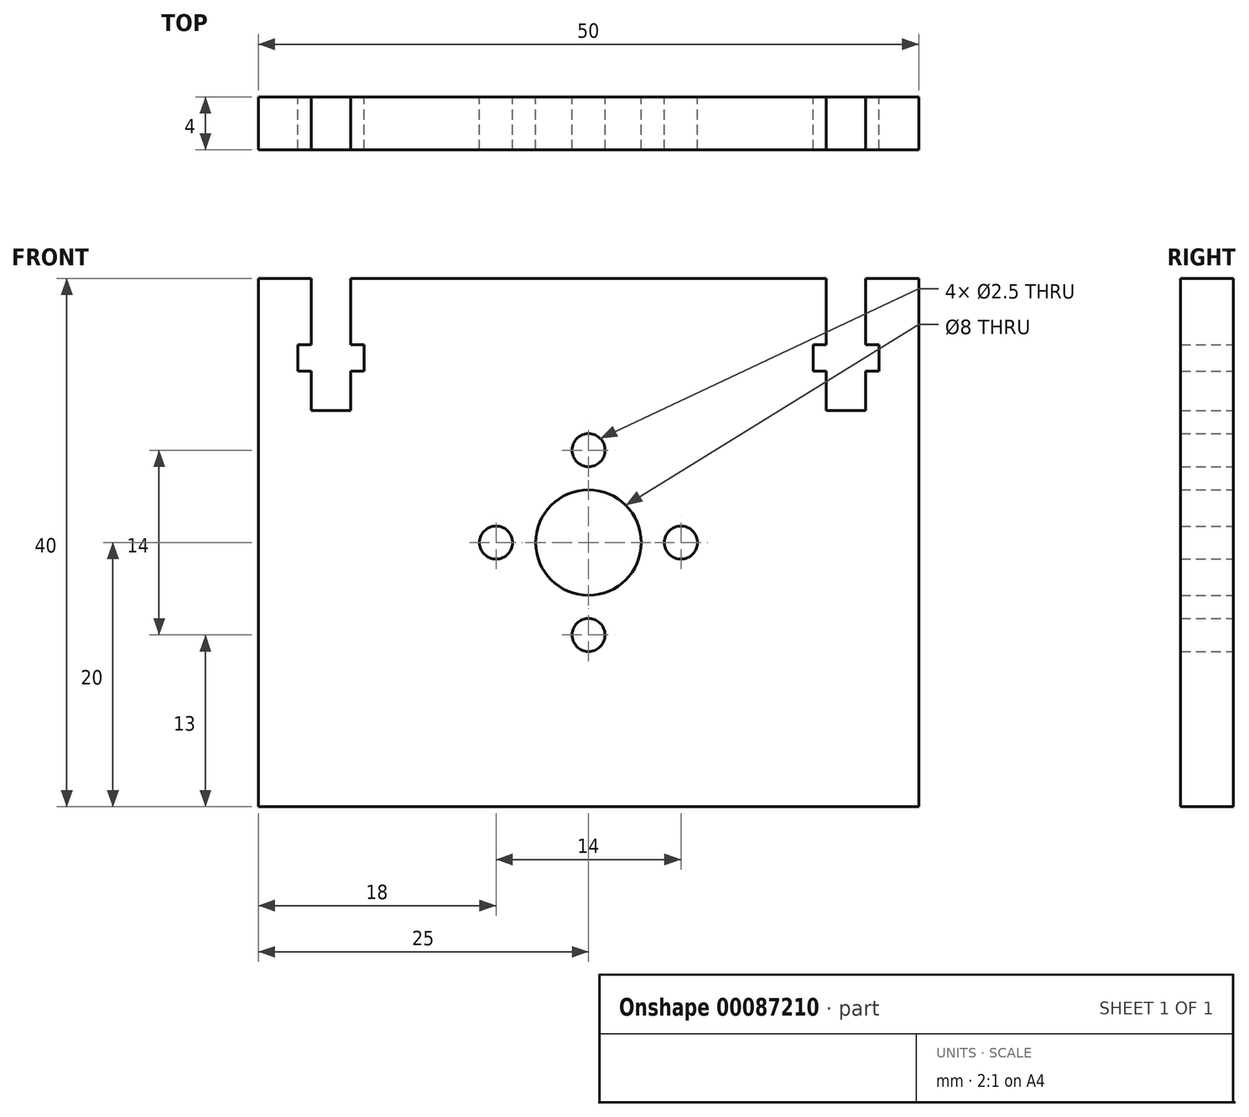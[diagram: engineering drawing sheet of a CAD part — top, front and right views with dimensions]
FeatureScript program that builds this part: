
annotation { "Feature Type Name" : "Feature", "Feature Type Description" : "" }
export const myFeature = defineFeature(function(context is Context, id is Id, definition is map)
    precondition{}
    {
        {
            var Q0;
            Q0=qCreatedBy(makeId("Front.planeOp"),FACE);
            var sketch = newSketch(context, id + "F0", { "sketchPlane" : qUnion([Q0])});
            skLineSegment(sketch, "E0.bottom", {"start": v(-46, 40) * mm, "end": v(-42, 40) * mm});
            skLineSegment(sketch, "E0.top", {"start": v(-46, 0) * mm, "end": v(4, 0) * mm});
            skLineSegment(sketch, "E0.left", {"start": v(-46, 40) * mm, "end": v(-46, 0) * mm});
            skLineSegment(sketch, "E0.right", {"start": v(4, 40) * mm, "end": v(4, 0) * mm});
            skLineSegment(sketch, "E1.left", {"start": v(4, 40) * mm, "end": v(4, 35) * mm});
            skLineSegment(sketch, "E1.right", {"start": v(0, 40) * mm, "end": v(0, 35) * mm});
            skLineSegment(sketch, "E2.top", {"start": v(1, 33) * mm, "end": v(0, 33) * mm});
            skLineSegment(sketch, "E2.right", {"start": v(-4, 35) * mm, "end": v(-4, 33) * mm});
            skLineSegment(sketch, "E3", {"start": v(-3, 40) * mm, "end": v(-3, 35) * mm});
            skLineSegment(sketch, "E4", {"start": v(-3, 33) * mm, "end": v(-3, 30) * mm});
            skLineSegment(sketch, "E5", {"start": v(0, 33) * mm, "end": v(0, 30) * mm});
            skLineSegment(sketch, "E6", {"start": v(0, 30) * mm, "end": v(-3, 30) * mm});
            skLineSegment(sketch, "E7.trimOffspring", {"start": v(-3, 35) * mm, "end": v(-4, 35) * mm});
            skLineSegment(sketch, "E8.trimOffspring", {"start": v(-3, 33) * mm, "end": v(-4, 33) * mm});
            skLineSegment(sketch, "E9.trimOffspring", {"start": v(0, 40) * mm, "end": v(4, 40) * mm});
            skLineSegment(sketch, "E10.top", {"start": v(-42, 30) * mm, "end": v(-39, 30) * mm});
            skLineSegment(sketch, "E10.left", {"start": v(-42, 40) * mm, "end": v(-42, 35) * mm});
            skLineSegment(sketch, "E10.right", {"start": v(-39, 40) * mm, "end": v(-39, 35) * mm});
            skPoint(sketch, "E11", {"position": v(-39, 35) * mm});
            skPoint(sketch, "E12", {"position": v(-39, 33) * mm});
            skLineSegment(sketch, "E13.bottom", {"start": v(-38, 35) * mm, "end": v(-39, 35) * mm});
            skLineSegment(sketch, "E13.top", {"start": v(-38, 33) * mm, "end": v(-39, 33) * mm});
            skLineSegment(sketch, "E13.left", {"start": v(-38, 35) * mm, "end": v(-38, 33) * mm});
            skLineSegment(sketch, "E13.right", {"start": v(-43, 35) * mm, "end": v(-43, 33) * mm});
            skLineSegment(sketch, "E14.trimOffspring", {"start": v(-42, 35) * mm, "end": v(-43, 35) * mm});
            skLineSegment(sketch, "E15.trimOffspring", {"start": v(-42, 33) * mm, "end": v(-42, 30) * mm});
            skLineSegment(sketch, "E16.trimOffspring", {"start": v(-39, 33) * mm, "end": v(-39, 30) * mm});
            skLineSegment(sketch, "E17.trimOffspring", {"start": v(-42, 33) * mm, "end": v(-43, 33) * mm});
            skPoint(sketch, "E18.end.orphan", {"position": v(-42, 35) * mm});
            skLineSegment(sketch, "E19.trimOffspring", {"start": v(-39, 40) * mm, "end": v(-3, 40) * mm});
            skCircle(sketch, "E20", {"center": v(-21, 20) * mm, "radius": 4 * mm});
            skCircle(sketch, "E21", {"center": v(-21, 27) * mm, "radius": 1.25 * mm});
            skCircle(sketch, "E22", {"center": v(-14, 20) * mm, "radius": 1.25 * mm});
            skCircle(sketch, "E23", {"center": v(-28, 20) * mm, "radius": 1.25 * mm});
            skCircle(sketch, "E24", {"center": v(-21, 13) * mm, "radius": 1.25 * mm});
            skPoint(sketch, "E25.trimOffspring.end.orphan", {"position": v(-21, 0) * mm});
            skPoint(sketch, "E26.orphan", {"position": v(-46, 20) * mm});
            skPoint(sketch, "E27.trimOffspring.end.orphan", {"position": v(4, 20) * mm});
            skPoint(sketch, "E28.orphan", {"position": v(-21, 40) * mm});
            skLineSegment(sketch, "E29", {"start": v(0, 35) * mm, "end": v(1, 35) * mm});
            skLineSegment(sketch, "E30", {"start": v(1, 35) * mm, "end": v(1, 33) * mm});
            skSolve(sketch);
        }
        {
            var Q0;
            Q0 = qSketchRegion(id + "F0", true);
            extrude(context, id + "F1", {"entities" : qUnion([Q0]), "depth" : 4 * mm});
        }
    });
